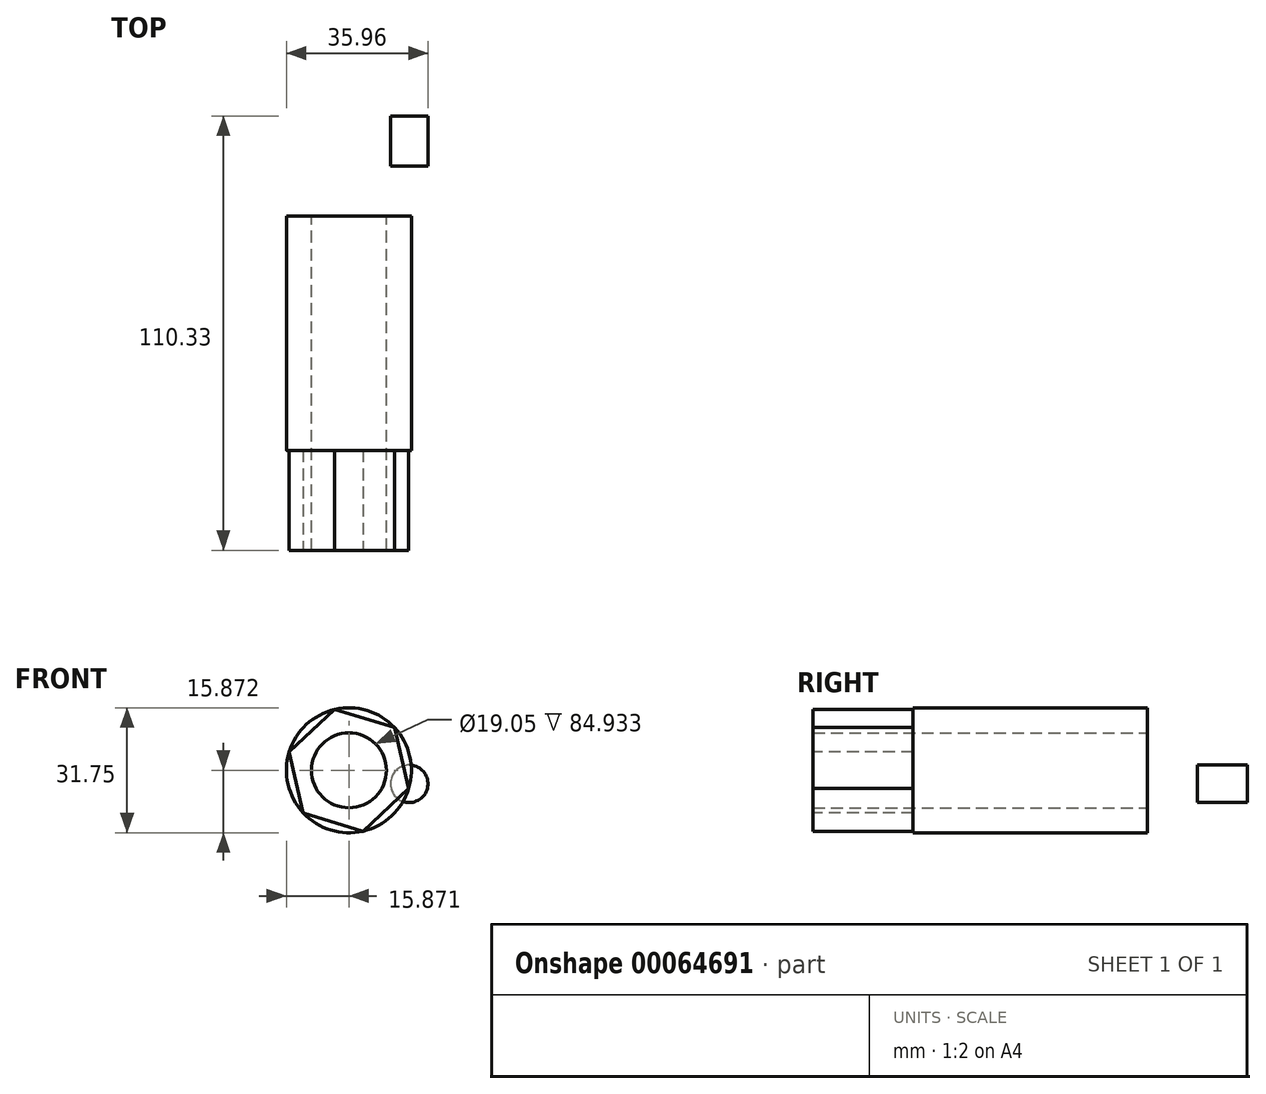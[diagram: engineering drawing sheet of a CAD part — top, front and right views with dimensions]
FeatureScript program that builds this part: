
annotation { "Feature Type Name" : "Feature", "Feature Type Description" : "" }
export const myFeature = defineFeature(function(context is Context, id is Id, definition is map)
    precondition{}
    {
        {
            var Q0;
            Q0=qCreatedBy(makeId("Front.planeOp"),FACE);
            var sketch = newSketch(context, id + "F0", { "sketchPlane" : qUnion([Q0])});
            skCircle(sketch, "E0", {"center": v(-30.65, 6.85) * mm, "radius": 9.52 * mm});
            skSolve(sketch);
        }
        {
            var Q0;
            Q0 = qSketchRegion(id + "F0", true);
            extrude(context, id + "F1", {"entities" : qUnion([Q0]), "depth" : 44.45 * mm});
        }
        {
            var Q0;
            Q0=makeQuery(id+"F1.opExtrude","CAP_FACE",FACE,{"disambiguationData":[OSD([sQuery(id+"F0.wireOp",EDGE,"E0")])],"isStart":false});
            extrude(context, id + "F2", {"entities" : qUnion([Q0]), "operationType" : NewBodyOperationType.REMOVE, "oppositeDirection" : true, "depth" : 19.05 * mm});
        }
        {
            var Q0;
            Q0=makeQuery(id+"F2.boolean.opBoolean","COPY",FACE,{"derivedFrom":makeQuery(id+"F2.opExtrude","CAP_FACE",FACE,{"disambiguationData":[OSD([sQuery(id+"F0.wireOp",EDGE,"E0")])],"isStart":false})});
            var sketch = newSketch(context, id + "F3", { "sketchPlane" : qUnion([Q0])});
            skCircle(sketch, "E1", {"center": v(-30.65, 6.85) * mm, "radius": 15.88 * mm});
            skSolve(sketch);
        }
        {
            var Q0;
            Q0=makeQuery(id+"F3.imprint","IMPRINT",FACE,{"disambiguationData":[TD([[makeQuery(id+"F3.imprint","IMPRINT",EDGE,{"derivedFrom":makeQuery(id+"F2.boolean.opBoolean","COPY",EDGE,{"derivedFrom":makeQuery(id+"F2.opExtrude","CAP_EDGE",EDGE,{"disambiguationData":[OSD([sQuery(id+"F0.wireOp",EDGE,"E0")])],"isStart":false})})}),1.0]])]});
            var Q1;
            Q1=makeQuery(id+"F3.imprint","IMPRINT",FACE,{"disambiguationData":[TD([[makeQuery(id+"F3.imprint","IMPRINT",EDGE,{"derivedFrom":sQuery(id+"F3.wireOp",EDGE,"E1")}),1.0]])]});
            extrude(context, id + "F4", {"entities" : qUnion([Q0, Q1]), "operationType" : NewBodyOperationType.ADD, "depth" : 84.93 * mm});
        }
        {
            var Q0;
            Q0=makeQuery(id+"F4.opExtrude","CAP_FACE",FACE,{"disambiguationData":[OSD([sQuery(id+"F3.wireOp",EDGE,"E1")])],"isStart":false});
            var sketch = newSketch(context, id + "F5", { "sketchPlane" : qUnion([Q0])});
            skCircle(sketch, "E2", {"center": v(-30.65, 6.85) * mm, "radius": 9.52 * mm});
            skSolve(sketch);
        }
        {
            var Q0;
            Q0 = qSketchRegion(id + "F5", true);
            extrude(context, id + "F6", {"entities" : qUnion([Q0]), "operationType" : NewBodyOperationType.REMOVE, "oppositeDirection" : true, "depth" : 44.45 * mm});
        }
        {
            var Q0;
            Q0=makeQuery(id+"F4.opExtrude","CAP_FACE",FACE,{"disambiguationData":[OSD([sQuery(id+"F3.wireOp",EDGE,"E1")])],"isStart":false});
            var sketch = newSketch(context, id + "F7", { "sketchPlane" : qUnion([Q0])});
            skCircle(sketch, "E3.cCircle", {"center": v(-30.65, 6.85) * mm, "radius": 15.88 * mm, "construction": true});
            skLineSegment(sketch, "E3.0", {"start": v(-19.05, 17.69) * mm, "end": v(-15.46, 2.23) * mm});
            skLineSegment(sketch, "E3.1", {"start": v(-15.46, 2.23) * mm, "end": v(-27.06, -8.61) * mm});
            skLineSegment(sketch, "E3.2", {"start": v(-27.06, -8.61) * mm, "end": v(-42.25, -3.98) * mm});
            skLineSegment(sketch, "E3.3", {"start": v(-42.25, -3.98) * mm, "end": v(-45.84, 11.48) * mm});
            skLineSegment(sketch, "E3.4", {"start": v(-45.84, 11.48) * mm, "end": v(-34.23, 22.32) * mm});
            skLineSegment(sketch, "E3.5", {"start": v(-34.23, 22.32) * mm, "end": v(-19.05, 17.69) * mm});
            skSolve(sketch);
        }
        {
            var Q0;
            {var subQ0=sQuery(id+"F7.wireOp",EDGE,"E3.4");Q0=makeQuery(id+"F7.imprint","IMPRINT",FACE,{"disambiguationData":[TD([[makeQuery(id+"F7.imprint","IMPRINT",EDGE,{"derivedFrom":subQ0}),1.0]])]});}
            var Q1;
            {var subQ0=sQuery(id+"F7.wireOp",EDGE,"E3.3");Q1=makeQuery(id+"F7.imprint","IMPRINT",FACE,{"disambiguationData":[TD([[makeQuery(id+"F7.imprint","IMPRINT",EDGE,{"derivedFrom":subQ0}),1.0]])]});}
            var Q2;
            {var subQ0=sQuery(id+"F7.wireOp",EDGE,"E3.2");Q2=makeQuery(id+"F7.imprint","IMPRINT",FACE,{"disambiguationData":[TD([[makeQuery(id+"F7.imprint","IMPRINT",EDGE,{"derivedFrom":subQ0}),1.0]])]});}
            var Q3;
            {var subQ0=sQuery(id+"F7.wireOp",EDGE,"E3.1");Q3=makeQuery(id+"F7.imprint","IMPRINT",FACE,{"disambiguationData":[TD([[makeQuery(id+"F7.imprint","IMPRINT",EDGE,{"derivedFrom":subQ0}),1.0]])]});}
            var Q4;
            {var subQ0=sQuery(id+"F7.wireOp",EDGE,"E3.0");Q4=makeQuery(id+"F7.imprint","IMPRINT",FACE,{"disambiguationData":[TD([[makeQuery(id+"F7.imprint","IMPRINT",EDGE,{"derivedFrom":subQ0}),1.0]])]});}
            var Q5;
            {var subQ0=sQuery(id+"F7.wireOp",EDGE,"E3.5");Q5=makeQuery(id+"F7.imprint","IMPRINT",FACE,{"disambiguationData":[TD([[makeQuery(id+"F7.imprint","IMPRINT",EDGE,{"derivedFrom":subQ0}),1.0]])]});}
            extrude(context, id + "F8", {"entities" : qUnion([Q0, Q1, Q2, Q3, Q4, Q5]), "operationType" : NewBodyOperationType.REMOVE, "oppositeDirection" : true, "depth" : 25.4 * mm});
        }
        {
            var Q0;
            Q0=makeQuery(id+"F1.opExtrude","SWEPT_BODY",BODY,{"disambiguationData":[OSD([sQuery(id+"F0.wireOp",EDGE,"E0")])]});
            var Q1;
            Q1=qCreatedBy(makeId("Origin.pointOp"),VERTEX);
            transform(context, id + "F9", {"entities" : qUnion([Q0]), "transformType" : TransformType.SCALE_UNIFORMLY, "scale" : .5, "scalePoint" : qUnion([Q1]), "makeCopy" : false});
        }
    });
